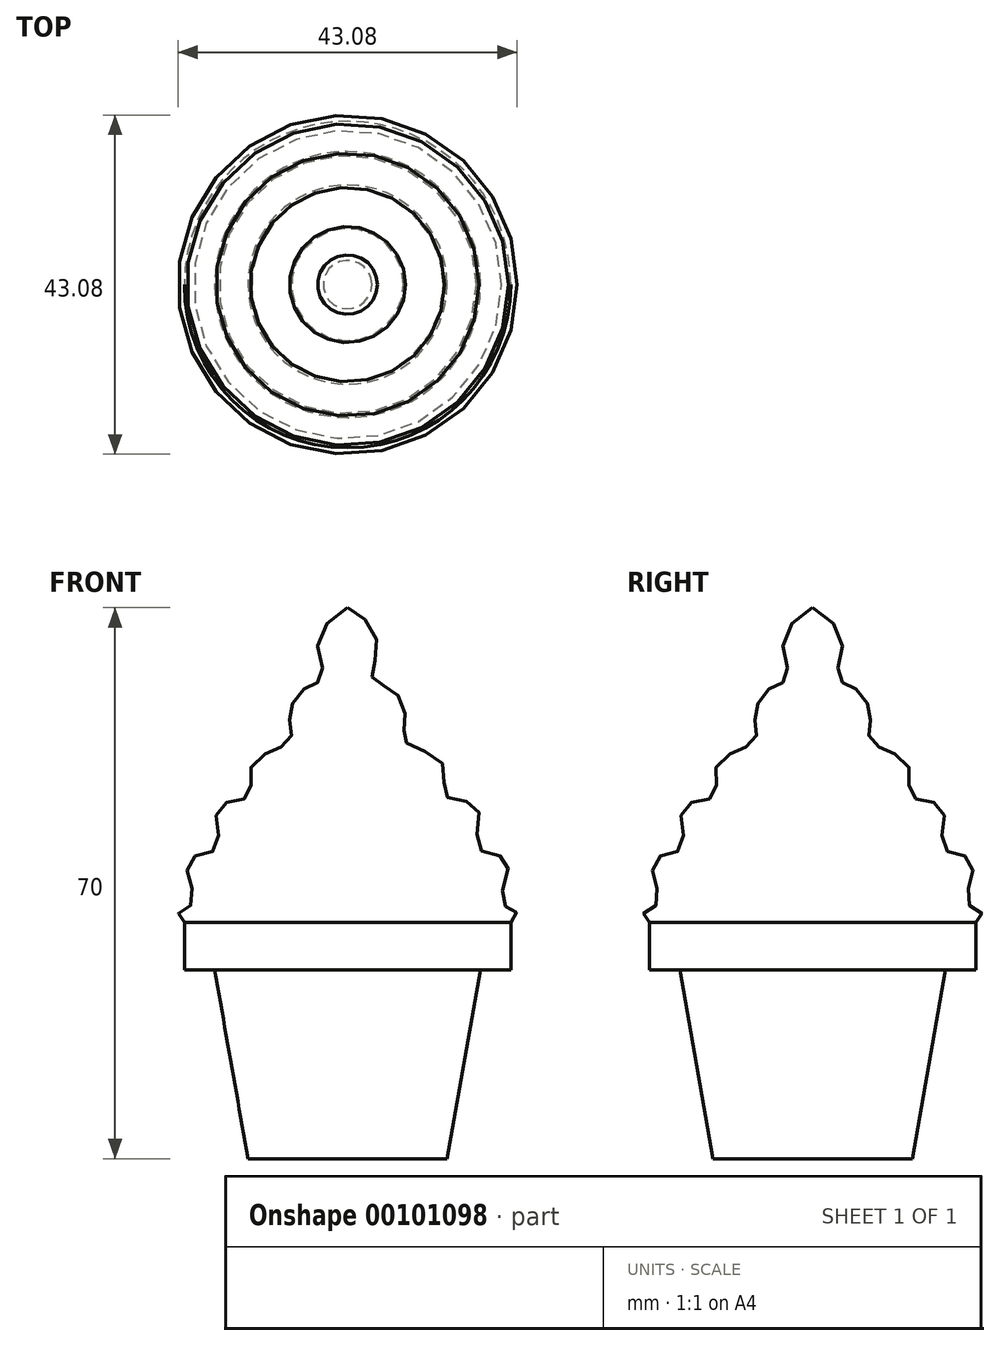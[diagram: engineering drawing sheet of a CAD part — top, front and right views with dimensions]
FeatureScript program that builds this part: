
annotation { "Feature Type Name" : "Feature", "Feature Type Description" : "" }
export const myFeature = defineFeature(function(context is Context, id is Id, definition is map)
    precondition{}
    {
        {
            var Q0;
            Q0=qCreatedBy(makeId("Front.planeOp"),FACE);
            var sketch = newSketch(context, id + "F0", { "sketchPlane" : qUnion([Q0])});
            skLineSegment(sketch, "E0", {"start": v(0, 0) * mm, "end": v(0, 70) * mm});
            skLineSegment(sketch, "E1", {"start": v(0, 0) * mm, "end": v(12.65, 0) * mm});
            skLineSegment(sketch, "E2", {"start": v(12.65, 0) * mm, "end": v(16.88, 24) * mm});
            skLineSegment(sketch, "E3", {"start": v(16.88, 24) * mm, "end": v(20.73, 24) * mm});
            skLineSegment(sketch, "E4", {"start": v(20.73, 24) * mm, "end": v(20.73, 30) * mm});
            skLineSegment(sketch, "E5", {"start": v(20.73, 30) * mm, "end": v(0, 30) * mm});
            skFitSpline(sketch, "E6", {"points": [v(0, 70) * mm, v(3.76, 65.5) * mm, v(3.16, 61.07) * mm, v(5.92, 59.39) * mm, v(7.34, 55.28) * mm, v(7.42, 52.9) * mm, v(12.1, 50.13) * mm, v(12.5, 46.09) * mm, v(16.45, 44.66) * mm, v(16.61, 39.43) * mm, v(20.26, 37.93) * mm, v(19.62, 32.62) * mm, v(21.37, 31.35) * mm, v(20.73, 30) * mm], "startDerivative": vector(47.94, -15.46) * mm, "endDerivative": vector(-53.04, -27.82) * mm});
            skSolve(sketch);
        }
        {
            var Q0;
            {var subQ2=sQuery(id+"F0.wireOp",EDGE,"E5");Q0=makeQuery(id+"F0.imprint","IMPRINT",FACE,{"disambiguationData":[TD([[makeQuery(id+"F0.imprint","IMPRINT",EDGE,{"derivedFrom":subQ2}),-1.0]])]});}
            var Q1;
            {var subQ0=sQuery(id+"F0.wireOp",EDGE,"E1");Q1=makeQuery(id+"F0.imprint","IMPRINT",FACE,{"disambiguationData":[TD([[makeQuery(id+"F0.imprint","IMPRINT",EDGE,{"derivedFrom":subQ0}),1.0]])]});}
            var Q2;
            Q2=sQuery(id+"F0.wireOp",EDGE,"E0");
            revolve(context, id + "F1", {"entities" : qUnion([Q0, Q1]), "axis" : qUnion([Q2]), "revolveType" : RevolveType.FULL});
        }
    });
